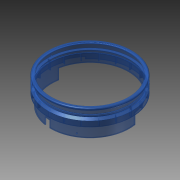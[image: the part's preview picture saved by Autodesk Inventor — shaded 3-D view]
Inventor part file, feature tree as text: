
AUTODESK INVENTOR PART (.ipt)
format: ipt  version: 2014 SP1 (Build 180222100, 222)  size: 598,528 bytes
history: native  units: in
note: dims shown in document units (in); Inventor stores cm internally (conversion verified against a paired STEP export)
features: extrude x9, sketch x8, reference x8, plane x4, revolve x2, pattern_circular x2, fillet x1
ambient origin geometry x8: Origin, YZ Plane, XZ Plane, XY Plane, X Axis, Y Axis, Z Axis, Center Point
bodies: Solid1 (feature_tree)
feature tree (34):
  sketch  "Sketch1"  dims[d0=5.625in d1=0.5in]
  revolve  "Revolution1"  [1 undecoded]
  extrude  "Extrusion1"  Depth=0.125in
  pattern_circular  "Circular Pattern3"  [2 undecoded]
  extrude  "Extrusion2"  Depth=0.0625in
  pattern_circular  "Circular Pattern4"  [2 undecoded]
  revolve  "Revolution4"  [1 undecoded]
  fillet  "Fillet1"  Radius=0.05in
  extrude  "Extrusion3"  TaperAngle=30.0deg  [1 undecoded]
  extrude  "Extrusion4"  Depth=0.0625in
  extrude  "Extrusion5"  Depth=0.0625in
  plane  "Work Plane1"
  extrude  "Extrusion6"  Depth=0.0625in
  plane  "Work Plane2"
  extrude  "Extrusion7"  Depth=0.0625in
  plane  "Work Plane3"
  extrude  "Extrusion8"  Depth=0.0625in
  plane  "Work Plane4"
  extrude  "Extrusion9"  Depth=0.0625in TaperAngle=0.0deg
  sketch  "Sketch2"  dims[d2=0.125in d3=0.125in]
  reference  "Reference1"
  sketch  "Sketch3"  dims[d4=0.1in]
  sketch  "Sketch4"  dims[d5=0.1in]
  reference  "Reference3"
  reference  "Reference4"
  reference  "Reference5"
  sketch  "Sketch5"  dims[d6=0.25in]
  reference  "Reference6"
  sketch  "Sketch6"  dims[d7=0.125in]
  reference  "Reference7"
  sketch  "Sketch7"  dims[d8=0.1in]
  reference  "Reference9"
  sketch  "Sketch8"  dims[d9=4.0in d11=0.375in d12=0.0625in d13=1.0in d14=1.3in d17=0.05in d18=30.0deg d19=0.3in d20=4.0in d21=0.0137in d22=0.05in d31=0.0625in d32=0.05in d33=0.0in d34=0.7874in d35=360.0deg d37=0.05in d38=0.0in d39=7.874in d40=360.0deg d42=90.0deg d43=0.125in d44=0.01in d45=0.3in d46=0.0in d47=7.96in d48=1.5in d49=0.0in d50=0.0618in d51=1.1681in d52=1.5in d53=0.0in d54=1.0in d55=0.0in d56=1.0in d57=0.0in d58=0.375in d59=0.0in d60=1.0in d61=0.0in]
  reference  "Reference10"
note: 7 required parameter values undecoded (feature->parameter linkage not recoverable at this tier; creation-order binding heuristic only, values carry confidence <= 0.55)